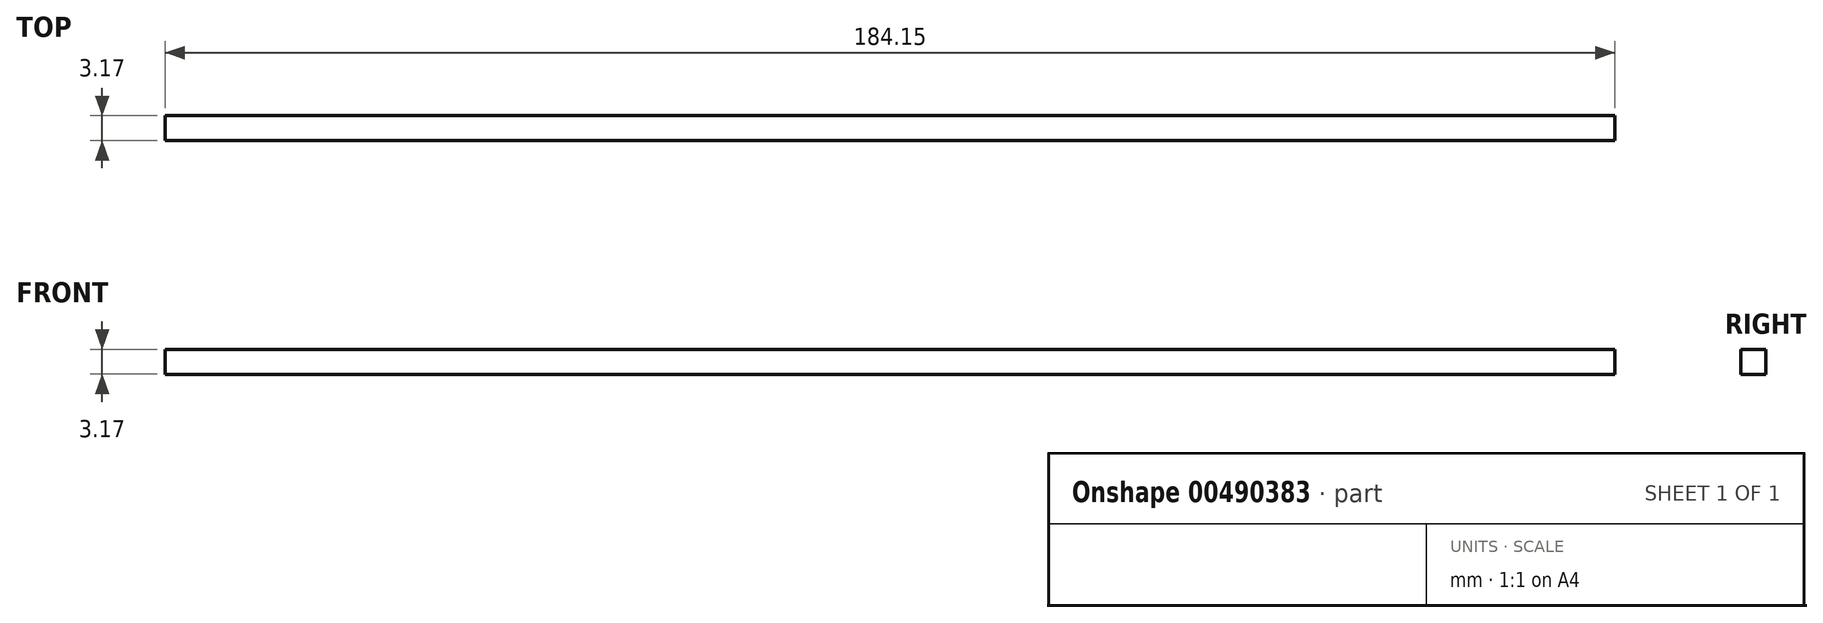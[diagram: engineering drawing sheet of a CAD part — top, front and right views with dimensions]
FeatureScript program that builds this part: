
annotation { "Feature Type Name" : "Feature", "Feature Type Description" : "" }
export const myFeature = defineFeature(function(context is Context, id is Id, definition is map)
    precondition{}
    {
        {
            var Q0;
            Q0=qCreatedBy(makeId("Right.planeOp"),FACE);
            var sketch = newSketch(context, id + "F0", { "sketchPlane" : qUnion([Q0])});
            skLineSegment(sketch, "E0.bottom", {"start": v(-62.96, 52.46) * mm, "end": v(-59.79, 52.46) * mm});
            skLineSegment(sketch, "E0.top", {"start": v(-62.96, 49.29) * mm, "end": v(-59.79, 49.29) * mm});
            skLineSegment(sketch, "E0.left", {"start": v(-62.96, 52.46) * mm, "end": v(-62.96, 49.29) * mm});
            skLineSegment(sketch, "E0.right", {"start": v(-59.79, 52.46) * mm, "end": v(-59.79, 49.29) * mm});
            skSolve(sketch);
        }
        {
            var Q0;
            Q0 = qSketchRegion(id + "F0", true);
            extrude(context, id + "F1", {"entities" : qUnion([Q0]), "depth" : 184.15 * mm});
        }
    });
